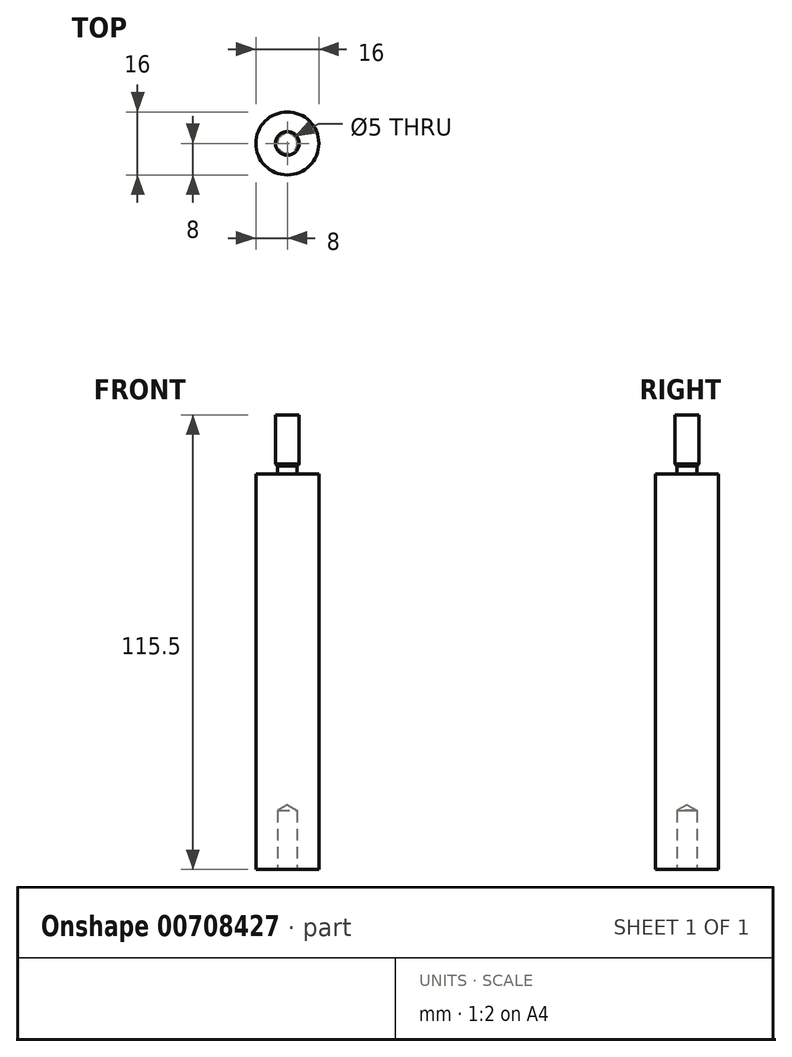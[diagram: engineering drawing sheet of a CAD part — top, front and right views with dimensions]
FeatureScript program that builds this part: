
annotation { "Feature Type Name" : "Feature", "Feature Type Description" : "" }
export const myFeature = defineFeature(function(context is Context, id is Id, definition is map)
    precondition{}
    {
        {
            var Q0;
            Q0=qCreatedBy(makeId("Front.planeOp"),FACE);
            var sketch = newSketch(context, id + "F0", { "sketchPlane" : qUnion([Q0])});
            skLineSegment(sketch, "E0", {"start": v(0, 15) * mm, "end": v(-3, 15) * mm});
            skLineSegment(sketch, "E1", {"start": v(-3, 15) * mm, "end": v(-3, 2.5) * mm});
            skLineSegment(sketch, "E2", {"start": v(-3, 2.5) * mm, "end": v(-2.5, 2) * mm});
            skLineSegment(sketch, "E3", {"start": v(-2.5, 2) * mm, "end": v(-2.5, 0) * mm});
            skLineSegment(sketch, "E4", {"start": v(-2.5, 0) * mm, "end": v(-8, 0) * mm});
            skLineSegment(sketch, "E5", {"start": v(-8, 0) * mm, "end": v(-8, -100.5) * mm});
            skLineSegment(sketch, "E6", {"start": v(-8, -100.5) * mm, "end": v(0, -100.5) * mm});
            skLineSegment(sketch, "E7", {"start": v(0, 71.4) * mm, "end": v(0, -147.73) * mm, "construction": true});
            skLineSegment(sketch, "E8", {"start": v(0, 15) * mm, "end": v(0, -100.5) * mm});
            skSolve(sketch);
        }
        {
            var Q0;
            Q0 = qSketchRegion(id + "F0", true);
            var Q1;
            Q1=sQuery(id+"F0.wireOp",EDGE,"E7");
            revolve(context, id + "F1", {"surfaceOperationType" : NewSurfaceOperationType.NEW, "entities" : qUnion([Q0]), "axis" : qUnion([Q1]), "revolveType" : RevolveType.FULL});
        }
        {
            var Q0;
            Q0=makeQuery(id+"F1.opRevolve","SWEPT_FACE",FACE,{"disambiguationData":[OSD([sQuery(id+"F0.wireOp",EDGE,"E6")])]});
            var sketch = newSketch(context, id + "F2", { "sketchPlane" : qUnion([Q0])});
            skPoint(sketch, "E9.0", {"position": v(0, 0) * mm});
            skSolve(sketch);
        }
        {
            var Q0;
            Q0=sQuery(id+"F2.wireOp",VERTEX,"E9.0");
            var Q1;
            Q1=makeQuery(id+"F1.opRevolve","SWEPT_BODY",BODY,{"disambiguationData":[OSD([sQuery(id+"F0.wireOp",EDGE,"E0"),sQuery(id+"F0.wireOp",EDGE,"E1"),sQuery(id+"F0.wireOp",EDGE,"E2"),sQuery(id+"F0.wireOp",EDGE,"E3"),sQuery(id+"F0.wireOp",EDGE,"E4"),sQuery(id+"F0.wireOp",EDGE,"E5"),sQuery(id+"F0.wireOp",EDGE,"E6"),sQuery(id+"F0.wireOp",EDGE,"E8")])]});
            hole(context, id + "F3", {"style" : HoleStyle.SIMPLE, "endStyle" : HoleEndStyle.BLIND, "standardTappedOrClearance" : lookupTablePath({ "standard" : "ISO", "engagement" : "75%", "pitch" : "1 mm", "size" : "M6", "type" : "Tapped" }), "standardBlindInLast" : lookupTablePath({ "standard" : "ISO", "engagement" : "75%", "pitch" : "1 mm", "size" : "M6", "type" : "Tapped" }), "holeDiameter" : 5 * mm, "majorDiameter" : 6 * mm, "showTappedDepth" : true, "holeDepth" : 15 * mm, "isTappedThrough" : true, "tappedDepth" : 12 * mm, "tapClearance" : 3, "locations" : qUnion([Q0]), "scope" : qUnion([Q1])});
        }
    });
